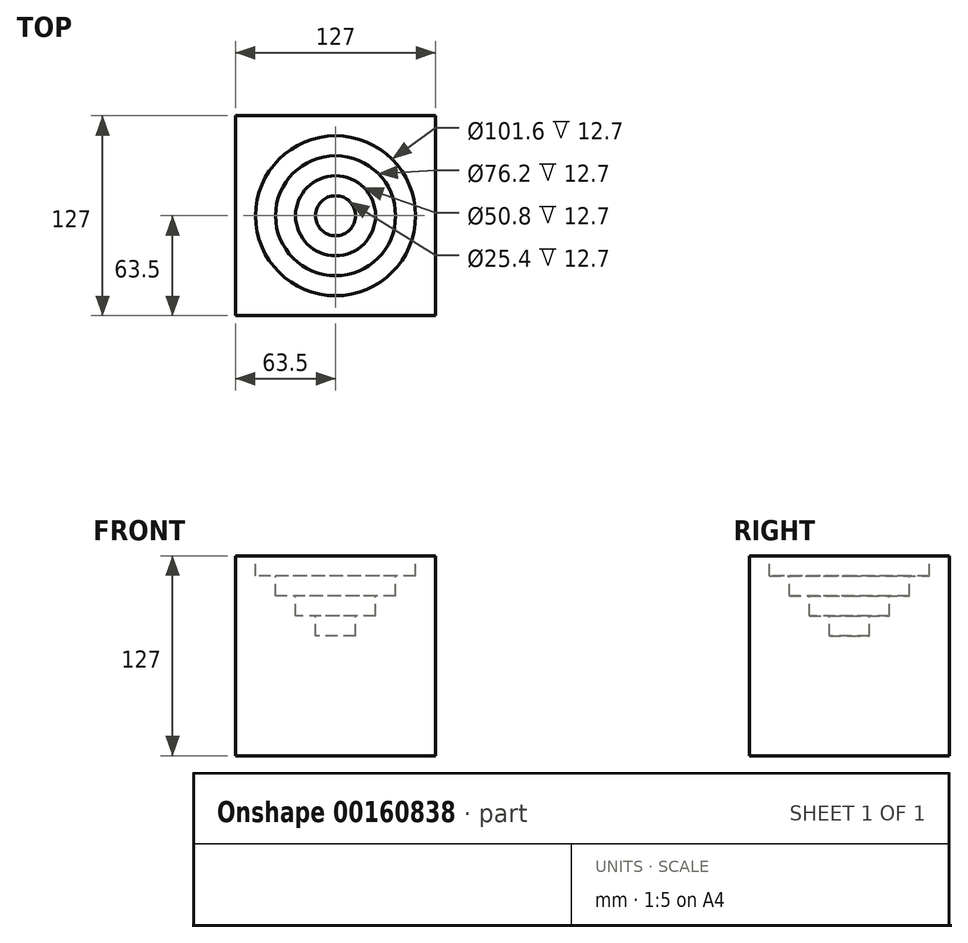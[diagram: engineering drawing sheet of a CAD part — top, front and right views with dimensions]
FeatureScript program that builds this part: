
annotation { "Feature Type Name" : "Feature", "Feature Type Description" : "" }
export const myFeature = defineFeature(function(context is Context, id is Id, definition is map)
    precondition{}
    {
        {
            var Q0;
            Q0=qCreatedBy(makeId("Front.planeOp"),FACE);
            var sketch = newSketch(context, id + "F0", { "sketchPlane" : qUnion([Q0])});
            skLineSegment(sketch, "E0.bottom", {"start": v(63.5, 63.5) * mm, "end": v(-63.5, 63.5) * mm});
            skLineSegment(sketch, "E0.top", {"start": v(63.5, -63.5) * mm, "end": v(-63.5, -63.5) * mm});
            skLineSegment(sketch, "E0.left", {"start": v(63.5, 63.5) * mm, "end": v(63.5, -63.5) * mm});
            skLineSegment(sketch, "E0.right", {"start": v(-63.5, 63.5) * mm, "end": v(-63.5, -63.5) * mm});
            skPoint(sketch, "E0.middle", {"position": v(0, 0) * mm});
            skSolve(sketch);
        }
        {
            var Q0;
            Q0=makeQuery(id+"F0.imprint","IMPRINT",FACE,{"disambiguationData":[TD([[makeQuery(id+"F0.imprint","IMPRINT",EDGE,{"derivedFrom":sQuery(id+"F0.wireOp",EDGE,"E0.bottom")}),1.0]])]});
            extrude(context, id + "F1", {"entities" : qUnion([Q0]), "endBound" : BoundingType.SYMMETRIC, "depth" : 127 * mm});
        }
        {
            var Q0;
            Q0=makeQuery(id+"F1.opExtrude","SWEPT_FACE",FACE,{"disambiguationData":[OSD([sQuery(id+"F0.wireOp",EDGE,"E0.bottom")])]});
            var sketch = newSketch(context, id + "F2", { "sketchPlane" : qUnion([Q0])});
            skCircle(sketch, "E1", {"center": v(0, 0) * mm, "radius": 50.8 * mm});
            skSolve(sketch);
        }
        {
            var Q0;
            Q0 = qSketchRegion(id + "F2", true);
            extrude(context, id + "F3", {"entities" : qUnion([Q0]), "operationType" : NewBodyOperationType.REMOVE, "oppositeDirection" : true, "depth" : 12.7 * mm});
        }
        {
            var Q0;
            Q0=makeQuery(id+"F3.boolean.opBoolean","COPY",FACE,{"derivedFrom":makeQuery(id+"F3.opExtrude","CAP_FACE",FACE,{"disambiguationData":[OSD([sQuery(id+"F2.wireOp",EDGE,"E1")])],"isStart":false})});
            var sketch = newSketch(context, id + "F4", { "sketchPlane" : qUnion([Q0])});
            skCircle(sketch, "E2", {"center": v(0, 0) * mm, "radius": 38.1 * mm});
            skSolve(sketch);
        }
        {
            var Q0;
            Q0 = qSketchRegion(id + "F4", true);
            extrude(context, id + "F5", {"entities" : qUnion([Q0]), "operationType" : NewBodyOperationType.REMOVE, "oppositeDirection" : true, "depth" : 12.7 * mm});
        }
        {
            var Q0;
            Q0=makeQuery(id+"F5.boolean.opBoolean","COPY",FACE,{"derivedFrom":makeQuery(id+"F5.opExtrude","CAP_FACE",FACE,{"disambiguationData":[OSD([sQuery(id+"F4.wireOp",EDGE,"E2")])],"isStart":false})});
            var sketch = newSketch(context, id + "F6", { "sketchPlane" : qUnion([Q0])});
            skCircle(sketch, "E3", {"center": v(0, 0) * mm, "radius": 25.4 * mm});
            skSolve(sketch);
        }
        {
            var Q0;
            Q0=makeQuery(id+"F6.imprint","IMPRINT",FACE,{"disambiguationData":[TD([[makeQuery(id+"F6.imprint","IMPRINT",EDGE,{"derivedFrom":sQuery(id+"F6.wireOp",EDGE,"E3")}),1.0]])]});
            extrude(context, id + "F7", {"entities" : qUnion([Q0]), "operationType" : NewBodyOperationType.REMOVE, "oppositeDirection" : true, "depth" : 12.7 * mm});
        }
        {
            var Q0;
            Q0=makeQuery(id+"F7.boolean.opBoolean","COPY",FACE,{"derivedFrom":makeQuery(id+"F7.opExtrude","CAP_FACE",FACE,{"disambiguationData":[OSD([sQuery(id+"F6.wireOp",EDGE,"E3")])],"isStart":false})});
            var sketch = newSketch(context, id + "F8", { "sketchPlane" : qUnion([Q0])});
            skCircle(sketch, "E4", {"center": v(0, 0) * mm, "radius": 12.7 * mm});
            skSolve(sketch);
        }
        {
            var Q0;
            Q0=makeQuery(id+"F8.imprint","IMPRINT",FACE,{"disambiguationData":[TD([[makeQuery(id+"F8.imprint","IMPRINT",EDGE,{"derivedFrom":sQuery(id+"F8.wireOp",EDGE,"E4")}),1.0]])]});
            extrude(context, id + "F9", {"entities" : qUnion([Q0]), "operationType" : NewBodyOperationType.REMOVE, "oppositeDirection" : true, "depth" : 12.7 * mm});
        }
    });
